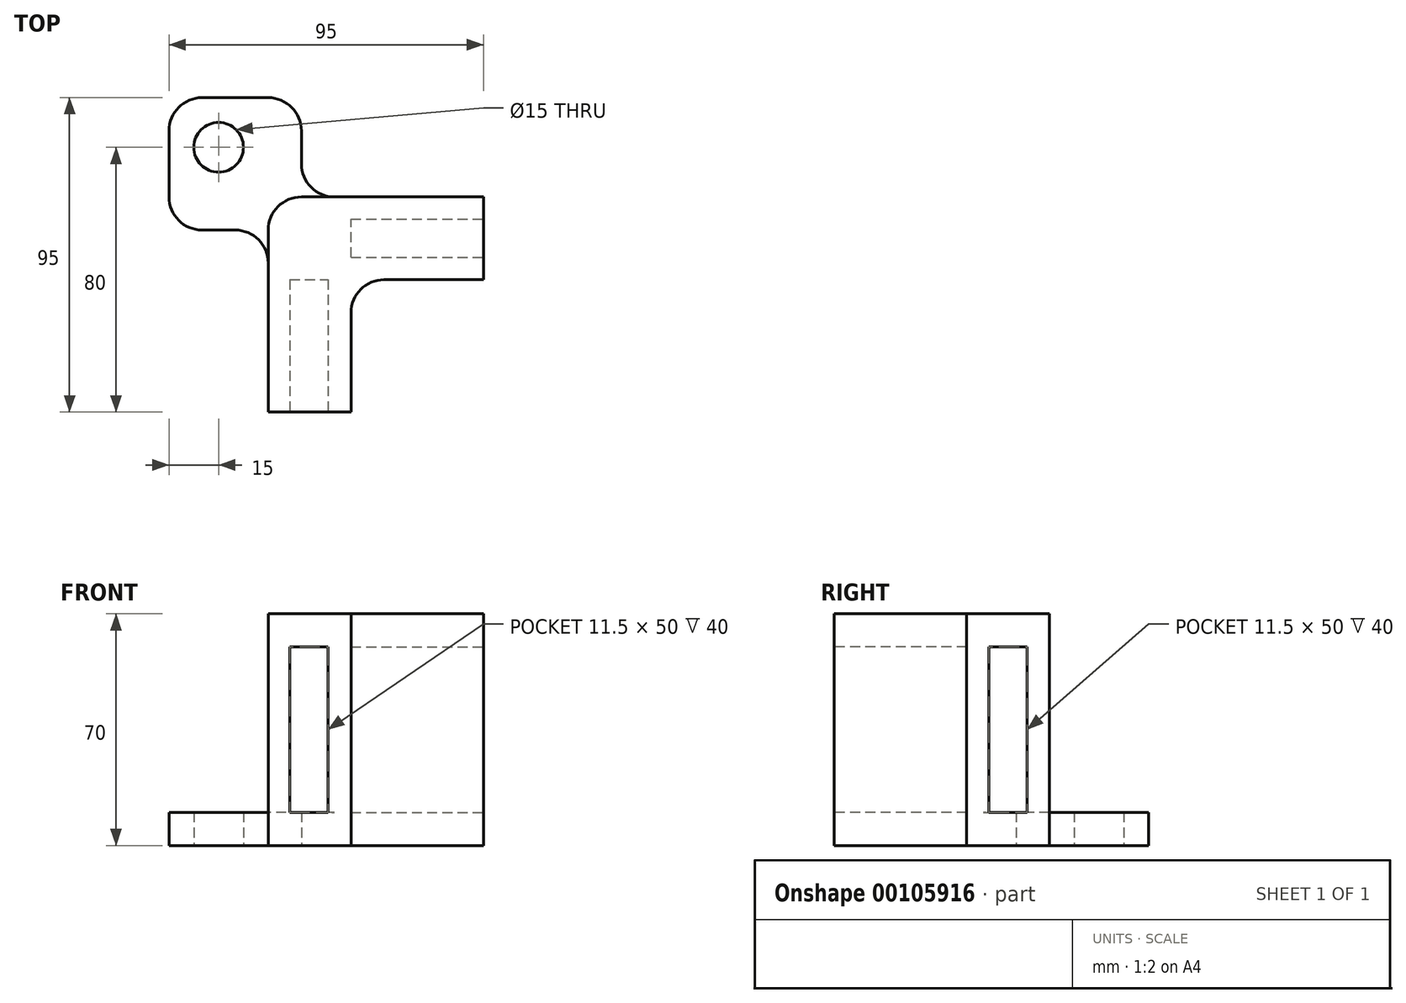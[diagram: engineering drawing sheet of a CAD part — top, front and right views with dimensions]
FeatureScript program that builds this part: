
annotation { "Feature Type Name" : "Feature", "Feature Type Description" : "" }
export const myFeature = defineFeature(function(context is Context, id is Id, definition is map)
    precondition{}
    {
        {
            var Q0;
            Q0=qCreatedBy(makeId("Top.planeOp"),FACE);
            var sketch = newSketch(context, id + "F0", { "sketchPlane" : qUnion([Q0])});
            skLineSegment(sketch, "E0", {"start": v(0, 0) * mm, "end": v(0, -65) * mm});
            skLineSegment(sketch, "E1", {"start": v(0, -65) * mm, "end": v(25, -65) * mm});
            skLineSegment(sketch, "E2", {"start": v(25, -65) * mm, "end": v(25, -25) * mm});
            skLineSegment(sketch, "E3", {"start": v(25, -25) * mm, "end": v(65, -25) * mm});
            skLineSegment(sketch, "E4", {"start": v(65, -25) * mm, "end": v(65, 0) * mm});
            skLineSegment(sketch, "E5", {"start": v(65, 0) * mm, "end": v(0, 0) * mm});
            skLineSegment(sketch, "E6", {"start": v(0, -10) * mm, "end": v(-20, -10) * mm});
            skLineSegment(sketch, "E7", {"start": v(10, 0) * mm, "end": v(10, 20) * mm});
            skLineSegment(sketch, "E8", {"start": v(0, 30) * mm, "end": v(-20, 30) * mm});
            skLineSegment(sketch, "E9", {"start": v(-30, 20) * mm, "end": v(-30, 0) * mm});
            skLineSegment(sketch, "E10", {"start": v(-15, -10) * mm, "end": v(-15, 30) * mm, "construction": true});
            skLineSegment(sketch, "E11", {"start": v(-30, 15) * mm, "end": v(10, 15) * mm, "construction": true});
            skCircle(sketch, "E12", {"center": v(-15, 15) * mm, "radius": 7.5 * mm});
            skPoint(sketch, "E13.visualSharp", {"position": v(-30, 30) * mm});
            skArc(sketch, "E13.filletArc", {"start": v(-20, 30) * mm, "mid": v(-27.07, 27.07) * mm, "end": v(-30, 20) * mm});
            skPoint(sketch, "E14.visualSharp", {"position": v(-30, -10) * mm});
            skArc(sketch, "E14.filletArc", {"start": v(-30, 0) * mm, "mid": v(-27.07, -7.07) * mm, "end": v(-20, -10) * mm});
            skPoint(sketch, "E15.visualSharp", {"position": v(10, 30) * mm});
            skArc(sketch, "E15.filletArc", {"start": v(10, 20) * mm, "mid": v(7.07, 27.07) * mm, "end": v(0, 30) * mm});
            skSolve(sketch);
        }
        {
            var Q0;
            Q0 = qSketchRegion(id + "F0", true);
            extrude(context, id + "F1", {"entities" : qUnion([Q0]), "depth" : 10 * mm});
        }
        {
            var Q0;
            Q0=makeQuery(id+"F1.opExtrude","CAP_FACE",FACE,{"disambiguationData":[OSD([sQuery(id+"F0.wireOp",EDGE,"E0"),sQuery(id+"F0.wireOp",EDGE,"E1"),sQuery(id+"F0.wireOp",EDGE,"E2"),sQuery(id+"F0.wireOp",EDGE,"E3"),sQuery(id+"F0.wireOp",EDGE,"E4"),sQuery(id+"F0.wireOp",EDGE,"E5"),sQuery(id+"F0.wireOp",EDGE,"E6"),sQuery(id+"F0.wireOp",EDGE,"E7"),sQuery(id+"F0.wireOp",EDGE,"E8"),sQuery(id+"F0.wireOp",EDGE,"E9"),sQuery(id+"F0.wireOp",EDGE,"E12"),sQuery(id+"F0.wireOp",EDGE,"E13.filletArc"),sQuery(id+"F0.wireOp",EDGE,"E14.filletArc"),sQuery(id+"F0.wireOp",EDGE,"E15.filletArc")])],"isStart":false});
            var sketch = newSketch(context, id + "F2", { "sketchPlane" : qUnion([Q0])});
            skLineSegment(sketch, "E16", {"start": v(10, 0) * mm, "end": v(0, 0) * mm});
            skLineSegment(sketch, "E17", {"start": v(0, 0) * mm, "end": v(0, -10) * mm});
            skSolve(sketch);
        }
        {
            var Q0;
            Q0=makeQuery(id+"F2.imprint","IMPRINT",FACE,{"disambiguationData":[TD([[makeQuery(id+"F2.imprint","IMPRINT",EDGE,{"derivedFrom":sQuery(id+"F2.wireOp",EDGE,"E16")}),1.0]])]});
            extrude(context, id + "F3", {"entities" : qUnion([Q0]), "operationType" : NewBodyOperationType.ADD, "depth" : 60 * mm});
        }
        {
            var Q0;
            Q0=makeQuery(id+"F3.opExtrude","CAP_EDGE",EDGE,{"disambiguationData":[OSD([sQuery(id+"F0.wireOp",EDGE,"E0"),sQuery(id+"F2.wireOp",EDGE,"E17")])],"isStart":true});
            var Q1;
            Q1=makeQuery(id+"F3.opExtrude","CAP_EDGE",EDGE,{"disambiguationData":[OSD([sQuery(id+"F0.wireOp",EDGE,"E5"),sQuery(id+"F2.wireOp",EDGE,"E16")])],"isStart":true});
            var Q2;
            Q2=makeQuery(id+"F1.opExtrude","SWEPT_EDGE",EDGE,{"disambiguationData":[OSD([sQuery(id+"F0.wireOp",EDGE,"E0"),sQuery(id+"F0.wireOp",EDGE,"E6")])]});
            var Q3;
            Q3=makeQuery(id+"F1.opExtrude","SWEPT_EDGE",EDGE,{"disambiguationData":[OSD([sQuery(id+"F0.wireOp",EDGE,"E5"),sQuery(id+"F0.wireOp",EDGE,"E7")])]});
            fillet(context, id + "F4", {"entities" : qUnion([Q0, Q1, Q2, Q3]), "radius" : 10 * mm, "tangentPropagation" : true, "allowEdgeOverflow" : false});
        }
        {
            var Q0;
            {var subQ0=sQuery(id+"F0.wireOp",EDGE,"E1");Q0=makeQuery(id+"F3.boolean.opBoolean","MERGE",FACE,{"derivedFrom":[makeQuery(id+"F1.opExtrude","SWEPT_FACE",FACE,{"disambiguationData":[OSD([subQ0])]}),makeQuery(id+"F3.opExtrude","SWEPT_FACE",FACE,{"disambiguationData":[OSD([subQ0])]})]});}
            var sketch = newSketch(context, id + "F5", { "sketchPlane" : qUnion([Q0])});
            skLineSegment(sketch, "E18.bottom", {"start": v(6.5, 60) * mm, "end": v(18, 60) * mm});
            skLineSegment(sketch, "E18.top", {"start": v(6.5, 10) * mm, "end": v(18, 10) * mm});
            skLineSegment(sketch, "E18.left", {"start": v(6.5, 60) * mm, "end": v(6.5, 10) * mm});
            skLineSegment(sketch, "E18.right", {"start": v(18, 60) * mm, "end": v(18, 10) * mm});
            skSolve(sketch);
        }
        {
            var Q0;
            Q0=makeQuery(id+"F5.imprint","IMPRINT",FACE,{"disambiguationData":[TD([[makeQuery(id+"F5.imprint","IMPRINT",EDGE,{"derivedFrom":sQuery(id+"F5.wireOp",EDGE,"E18.bottom")}),-1.0]])]});
            var Q1;
            {var subQ0=sQuery(id+"F0.wireOp",EDGE,"E3");Q1=makeQuery(id+"F3.boolean.opBoolean","MERGE",FACE,{"derivedFrom":[makeQuery(id+"F1.opExtrude","SWEPT_FACE",FACE,{"disambiguationData":[OSD([subQ0])]}),makeQuery(id+"F3.opExtrude","SWEPT_FACE",FACE,{"disambiguationData":[OSD([subQ0])]})]});}
            extrude(context, id + "F6", {"entities" : qUnion([Q0]), "operationType" : NewBodyOperationType.REMOVE, "endBound" : BoundingType.UP_TO_SURFACE, "oppositeDirection" : true, "endBoundEntityFace" : qUnion([Q1]), "depth" : 25 * mm});
        }
        {
            var Q0;
            {var subQ0=sQuery(id+"F0.wireOp",EDGE,"E4");Q0=makeQuery(id+"F3.boolean.opBoolean","MERGE",FACE,{"derivedFrom":[makeQuery(id+"F1.opExtrude","SWEPT_FACE",FACE,{"disambiguationData":[OSD([subQ0])]}),makeQuery(id+"F3.opExtrude","SWEPT_FACE",FACE,{"disambiguationData":[OSD([subQ0])]})]});}
            var sketch = newSketch(context, id + "F7", { "sketchPlane" : qUnion([Q0])});
            skLineSegment(sketch, "E19.bottom", {"start": v(-18.25, 60) * mm, "end": v(-6.75, 60) * mm});
            skLineSegment(sketch, "E19.top", {"start": v(-18.25, 10) * mm, "end": v(-6.75, 10) * mm});
            skLineSegment(sketch, "E19.left", {"start": v(-18.25, 60) * mm, "end": v(-18.25, 10) * mm});
            skLineSegment(sketch, "E19.right", {"start": v(-6.75, 60) * mm, "end": v(-6.75, 10) * mm});
            skSolve(sketch);
        }
        {
            var Q0;
            Q0=makeQuery(id+"F7.imprint","IMPRINT",FACE,{"disambiguationData":[TD([[makeQuery(id+"F7.imprint","IMPRINT",EDGE,{"derivedFrom":sQuery(id+"F7.wireOp",EDGE,"E19.bottom")}),-1.0]])]});
            var Q1;
            {var subQ0=sQuery(id+"F0.wireOp",EDGE,"E2");Q1=makeQuery(id+"F3.boolean.opBoolean","MERGE",FACE,{"derivedFrom":[makeQuery(id+"F1.opExtrude","SWEPT_FACE",FACE,{"disambiguationData":[OSD([subQ0])]}),makeQuery(id+"F3.opExtrude","SWEPT_FACE",FACE,{"disambiguationData":[OSD([subQ0])]})]});}
            extrude(context, id + "F8", {"entities" : qUnion([Q0]), "operationType" : NewBodyOperationType.REMOVE, "endBound" : BoundingType.UP_TO_SURFACE, "oppositeDirection" : true, "endBoundEntityFace" : qUnion([Q1]), "depth" : 25 * mm});
        }
        {
            var Q0;
            Q0=makeQuery(id+"F3.opExtrude","SWEPT_EDGE",EDGE,{"disambiguationData":[OSD([sQuery(id+"F2.wireOp",EDGE,"E16"),sQuery(id+"F2.wireOp",EDGE,"E17")])]});
            var Q1;
            {var subQ0=sQuery(id+"F0.wireOp",EDGE,"E3");var subQ1=sQuery(id+"F0.wireOp",EDGE,"E2");Q1=makeQuery(id+"F3.boolean.opBoolean","MERGE",EDGE,{"derivedFrom":[makeQuery(id+"F1.opExtrude","SWEPT_EDGE",EDGE,{"disambiguationData":[OSD([subQ1,subQ0])]}),makeQuery(id+"F3.opExtrude","SWEPT_EDGE",EDGE,{"disambiguationData":[OSD([subQ1,subQ0])]})]});}
            fillet(context, id + "F9", {"entities" : qUnion([Q0, Q1]), "radius" : 10 * mm, "tangentPropagation" : true, "allowEdgeOverflow" : false});
        }
    });
